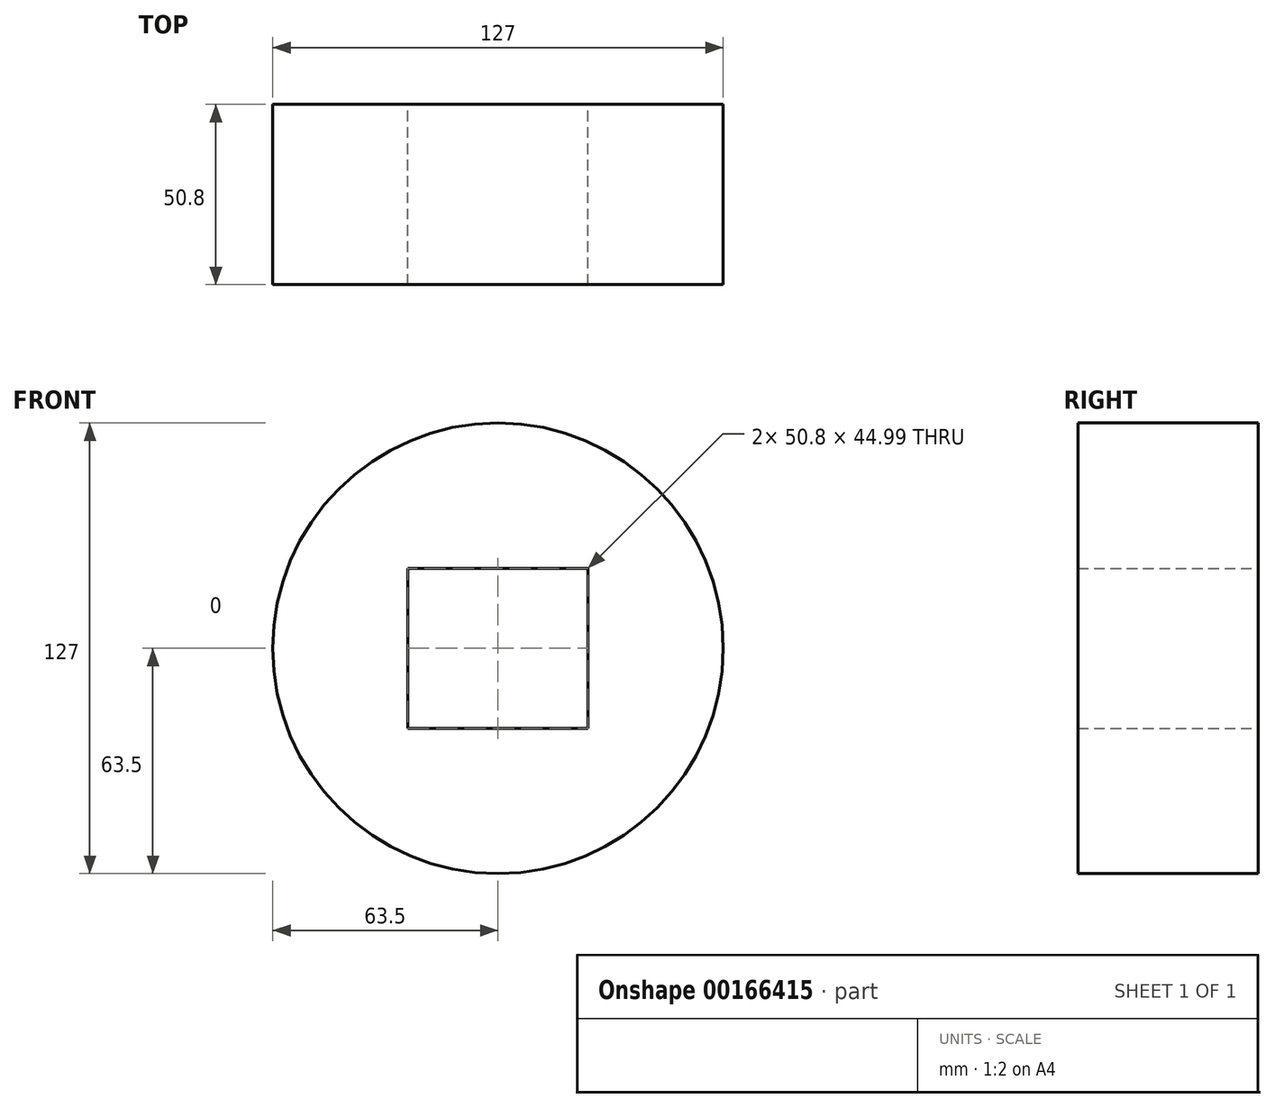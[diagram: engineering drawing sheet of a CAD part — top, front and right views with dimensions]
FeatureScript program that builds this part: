
annotation { "Feature Type Name" : "Feature", "Feature Type Description" : "" }
export const myFeature = defineFeature(function(context is Context, id is Id, definition is map)
    precondition{}
    {
        {
            var Q0;
            Q0=qCreatedBy(makeId("Front.planeOp"),FACE);
            var sketch = newSketch(context, id + "F0", { "sketchPlane" : qUnion([Q0])});
            skCircle(sketch, "E0", {"center": v(0, 0) * mm, "radius": 63.5 * mm});
            skLineSegment(sketch, "E1.bottom", {"start": v(25.4, 22.5) * mm, "end": v(-25.4, 22.5) * mm});
            skLineSegment(sketch, "E1.top", {"start": v(25.4, -22.5) * mm, "end": v(-25.4, -22.5) * mm});
            skLineSegment(sketch, "E1.left", {"start": v(25.4, 22.5) * mm, "end": v(25.4, -22.5) * mm});
            skLineSegment(sketch, "E1.right", {"start": v(-25.4, 22.5) * mm, "end": v(-25.4, -22.5) * mm});
            skSolve(sketch);
        }
        {
            var Q0;
            Q0 = qSketchRegion(id + "F0", true);
            extrude(context, id + "F1", {"entities" : qUnion([Q0]), "depth" : 50.8 * mm});
        }
    });
